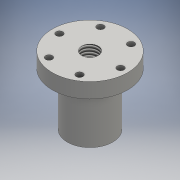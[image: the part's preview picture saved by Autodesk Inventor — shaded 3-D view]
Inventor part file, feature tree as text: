
AUTODESK INVENTOR PART (.ipt)
format: ipt  version: 2016 (Build 200138000, 138)  size: 128,512 bytes
history: native  units: mm
features: sketch x3, extrude x2, revolve x1, thread x1
ambient origin geometry x8: Origin, YZ Plane, XZ Plane, XY Plane, X Axis, Y Axis, Z Axis, Center Point
bodies: Solid1 (feature_tree)
feature tree (7):
  revolve  "Revolution1"  [1 undecoded]
  extrude  "Extrusion1"  Depth=35.0mm
  extrude  "Extrusion2"  TaperAngle=90.0deg  [1 undecoded]
  thread  "Thread1"  [1 undecoded]
  sketch  "Sketch1"  dims[d3=25.0mm d4=10.0mm]
  sketch  "Sketch2"  dims[d5=10.0mm d6=35.0mm]
  sketch  "Sketch3"  dims[d7=15.0mm d8=90.0deg d12=4.5mm d13=60.0mm d15=360.0deg d17=10.0mm d18=0.0mm d19=11.0mm d27=10.0mm d28=0.0mm d29=10.0mm d30=0.0mm]
note: 3 required parameter values undecoded (feature->parameter linkage not recoverable at this tier; creation-order binding heuristic only, values carry confidence <= 0.55)